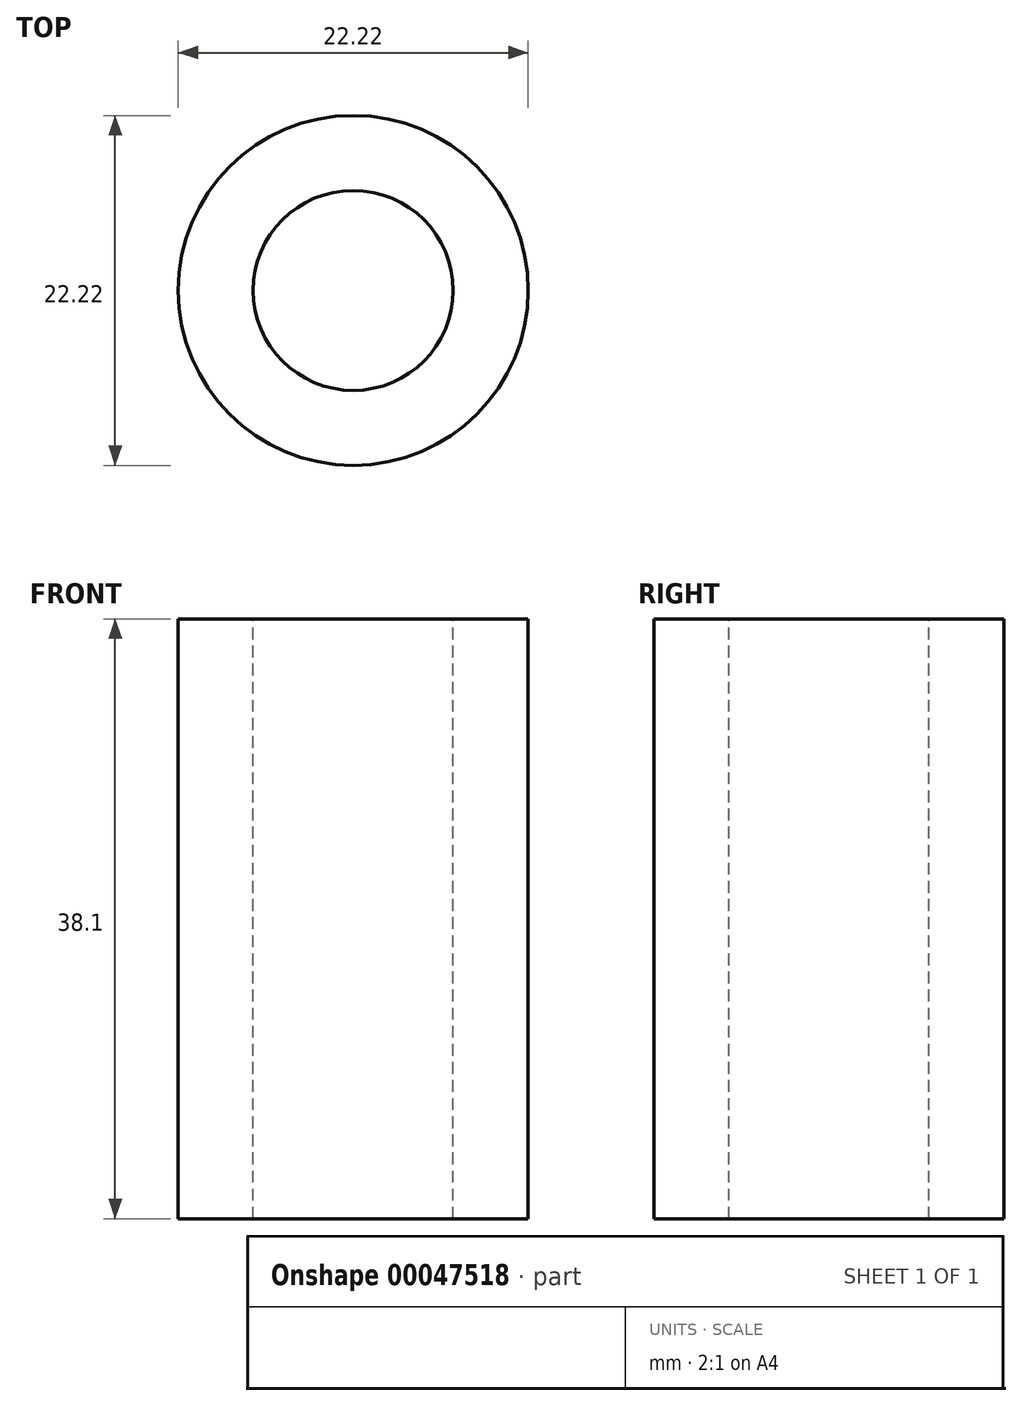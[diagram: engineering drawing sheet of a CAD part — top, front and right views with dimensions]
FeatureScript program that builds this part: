
annotation { "Feature Type Name" : "Feature", "Feature Type Description" : "" }
export const myFeature = defineFeature(function(context is Context, id is Id, definition is map)
    precondition{}
    {
        {
            var Q0;
            Q0=qCreatedBy(makeId("Top.planeOp"),FACE);
            var sketch = newSketch(context, id + "F0", { "sketchPlane" : qUnion([Q0])});
            skCircle(sketch, "E0", {"center": v(0, 0) * mm, "radius": 11.11 * mm});
            skSolve(sketch);
        }
        {
            var Q0;
            Q0=makeQuery(id+"F0.imprint","IMPRINT",FACE,{"disambiguationData":[TD([[makeQuery(id+"F0.imprint","IMPRINT",EDGE,{"derivedFrom":sQuery(id+"F0.wireOp",EDGE,"E0")}),1.0]])]});
            extrude(context, id + "F1", {"entities" : qUnion([Q0]), "endBound" : BoundingType.SYMMETRIC, "depth" : 38.1 * mm});
        }
        {
            var Q0;
            Q0=qCreatedBy(makeId("Top.planeOp"),FACE);
            var sketch = newSketch(context, id + "F2", { "sketchPlane" : qUnion([Q0])});
            skCircle(sketch, "E1", {"center": v(0, 0) * mm, "radius": 6.35 * mm});
            skSolve(sketch);
        }
        {
            var Q0;
            Q0 = qSketchRegion(id + "F2", true);
            extrude(context, id + "F3", {"entities" : qUnion([Q0]), "operationType" : NewBodyOperationType.REMOVE, "endBound" : BoundingType.SYMMETRIC, "oppositeDirection" : true, "depth" : 38.1 * mm});
        }
    });
